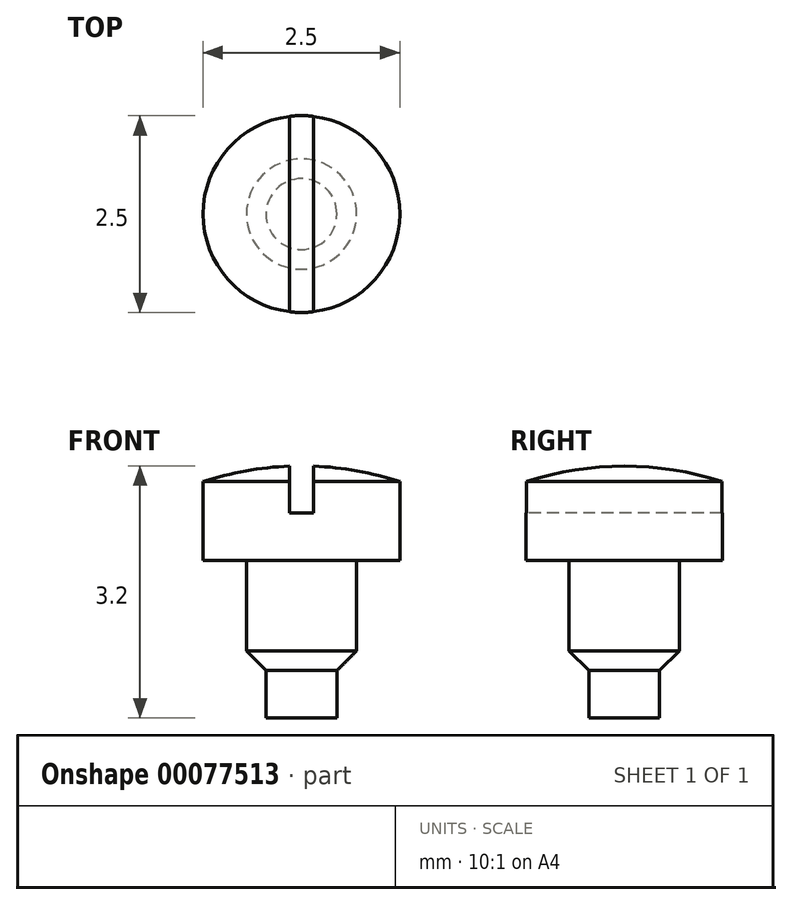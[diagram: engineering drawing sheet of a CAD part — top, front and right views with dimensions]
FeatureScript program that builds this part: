
annotation { "Feature Type Name" : "Feature", "Feature Type Description" : "" }
export const myFeature = defineFeature(function(context is Context, id is Id, definition is map)
    precondition{}
    {
        {
            var Q0;
            Q0=qCreatedBy(makeId("Front.planeOp"),FACE);
            var sketch = newSketch(context, id + "F0", { "sketchPlane" : qUnion([Q0])});
            skLineSegment(sketch, "E0", {"start": v(0, 0) * mm, "end": v(0.45, 0) * mm});
            skLineSegment(sketch, "E1", {"start": v(0.45, 0) * mm, "end": v(0.45, 0.6) * mm});
            skLineSegment(sketch, "E2", {"start": v(0.45, 0.6) * mm, "end": v(0.7, 0.85) * mm});
            skLineSegment(sketch, "E3", {"start": v(0.7, 0.85) * mm, "end": v(0.7, 2) * mm});
            skLineSegment(sketch, "E4", {"start": v(0.7, 2) * mm, "end": v(1.25, 2) * mm});
            skLineSegment(sketch, "E5", {"start": v(1.25, 2) * mm, "end": v(1.25, 3) * mm});
            skLineSegment(sketch, "E6", {"start": v(1.25, 3) * mm, "end": v(0, 3) * mm});
            skLineSegment(sketch, "E7", {"start": v(0, 3) * mm, "end": v(0, 0) * mm});
            skArc(sketch, "E8", {"start": v(1.25, 3) * mm, "mid": v(0.63, 3.15) * mm, "end": v(0, 3.2) * mm});
            skLineSegment(sketch, "E9", {"start": v(0, 3.2) * mm, "end": v(0, 3) * mm});
            skSolve(sketch);
        }
        {
            var Q0;
            {var subQ0=makeQuery(id+"F0.imprint","IMPRINT",EDGE,{"derivedFrom":sQuery(id+"F0.wireOp",EDGE,"E6")});Q0=qUnion([makeQuery(id+"F0.imprint","IMPRINT",FACE,{"disambiguationData":[TD([[makeQuery(id+"F0.imprint","IMPRINT",EDGE,{"derivedFrom":sQuery(id+"F0.wireOp",EDGE,"E0")}),1.0]])]}),makeQuery(id+"F0.imprint","IMPRINT",FACE,{"disambiguationData":[TD([[subQ0,-1.0]])]})]);}
            var Q1;
            Q1=sQuery(id+"F0.wireOp",EDGE,"E7");
            revolve(context, id + "F1", {"entities" : qUnion([Q0]), "axis" : qUnion([Q1]), "revolveType" : RevolveType.FULL});
        }
        {
            var Q0;
            Q0=qCreatedBy(makeId("Front.planeOp"),FACE);
            var sketch = newSketch(context, id + "F2", { "sketchPlane" : qUnion([Q0])});
            skLineSegment(sketch, "E10", {"start": v(-0.15, 2.6) * mm, "end": v(0.15, 2.6) * mm});
            skPoint(sketch, "E11", {"position": v(0, 2.6) * mm});
            skLineSegment(sketch, "E12", {"start": v(-0.15, 2.6) * mm, "end": v(-0.15, 3.25) * mm});
            skLineSegment(sketch, "E13", {"start": v(-0.15, 3.25) * mm, "end": v(0.15, 3.25) * mm});
            skLineSegment(sketch, "E14", {"start": v(0.15, 3.25) * mm, "end": v(0.15, 2.6) * mm});
            skSolve(sketch);
        }
        {
            var Q0;
            Q0=makeQuery(id+"F2.imprint","IMPRINT",FACE,{"disambiguationData":[TD([[makeQuery(id+"F2.imprint","IMPRINT",EDGE,{"derivedFrom":sQuery(id+"F2.wireOp",EDGE,"E10")}),1.0]])]});
            extrude(context, id + "F3", {"entities" : qUnion([Q0]), "operationType" : NewBodyOperationType.REMOVE, "oppositeDirection" : true, "depth" : 25 * mm, "symmetric" : true});
        }
    });
